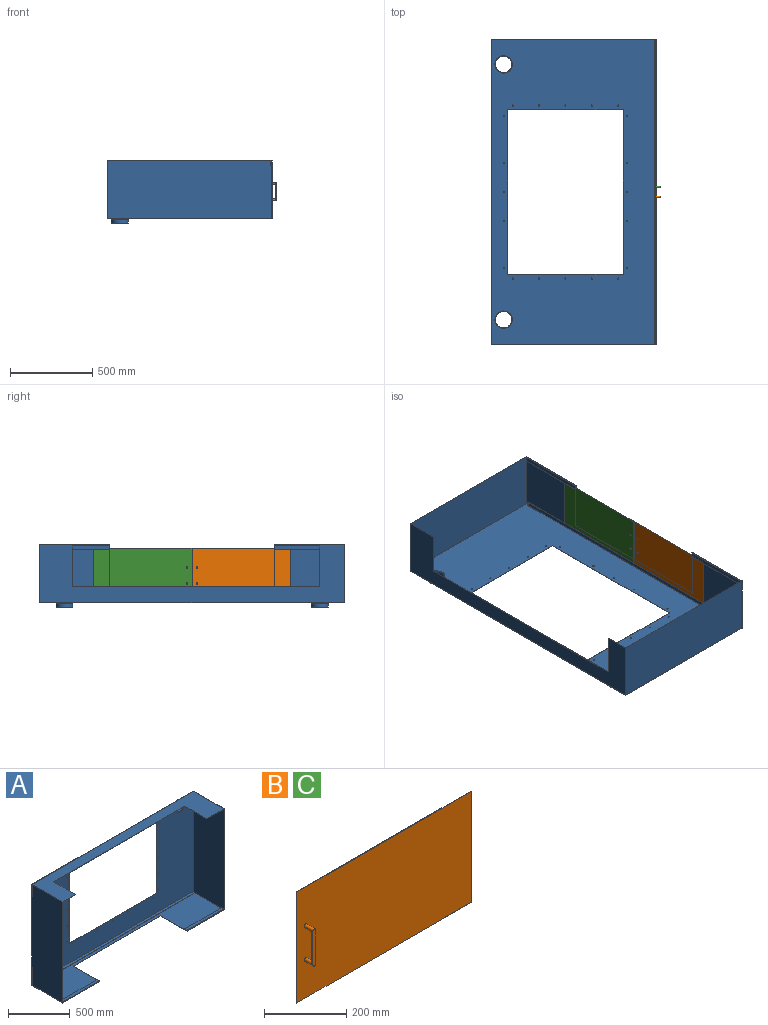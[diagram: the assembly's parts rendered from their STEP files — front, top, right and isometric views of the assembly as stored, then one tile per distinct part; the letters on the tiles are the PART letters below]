
ASSEMBLY  parts=3 mates=2
PART A: 67 faces, bbox 1850x376.5x1000 mm
  f0: plane 1847x350mm, normal (0,0,1), area 343690mm2, adj f2,f3,f34,f36,f37,f41,f42,f43
  f1: plane 1850x351.5mm, normal (0,0,-1), area 348775mm2, adj f2,f4,f5,f33,f37,f41,f42,f43
  f2: plane 1000x425mm, normal (0,-1,0), area 5373mm2, adj f0,f1,f5,f32,f35,f36,f39,f43
  f3: plane 1847x997mm, normal (0,-1,0), area 1117616.6mm2, adj f0,f6,f7,f8,f9,f10,f11,f12
  f4: plane 1000x351.5mm, normal (-1,0,0), area 351500mm2, adj f1,f32,f33,f37
  f5: plane 1000x351.5mm, normal (1,0,0), area 351500mm2, adj f1,f2,f32,f33
  f6: plane 700x1.5mm, normal (1,0,0), area 1050mm2, adj f3,f7,f31,f33
  f7: plane 1000x1.5mm, normal (0,0,-1), area 1500mm2, adj f3,f6,f8,f33
  f8: plane 700x1.5mm, normal (-1,0,0), area 1050mm2, adj f3,f7,f31,f33
  f9: cylinder r=3.5mm len=7mm, axis (0,1,0), area 33mm2, adj f3,f33
  f10: cylinder r=3.5mm len=7mm, axis (0,1,0), area 33mm2, adj f3,f33
  f11: cylinder r=3.5mm len=7mm, axis (0,1,0), area 33mm2, adj f3,f33
  f12: cylinder r=3.5mm len=7mm, axis (0,1,0), area 33mm2, adj f3,f33
  f13: cylinder r=3.5mm len=7mm, axis (0,1,0), area 33mm2, adj f3,f33
  f14: cylinder r=3.5mm len=7mm, axis (0,1,0), area 33mm2, adj f3,f33
  f15: cylinder r=3.5mm len=7mm, axis (0,1,0), area 33mm2, adj f3,f33
  f16: cylinder r=3.5mm len=7mm, axis (0,1,0), area 33mm2, adj f3,f33
  f17: cylinder r=3.5mm len=7mm, axis (0,1,0), area 33mm2, adj f3,f33
  f18: cylinder r=3.5mm len=7mm, axis (0,1,0), area 33mm2, adj f3,f33
  f19: cylinder r=50mm len=100mm, axis (0,1,0), area 7382.7mm2, adj f45,f48
  f20: cylinder r=50mm len=100mm, axis (0,1,0), area 7382.7mm2, adj f47,f49
  f21: cylinder r=3.5mm len=7mm, axis (0,1,0), area 33mm2, adj f3,f33
  f22: cylinder r=3.5mm len=7mm, axis (0,1,0), area 33mm2, adj f3,f33
  f23: cylinder r=3.5mm len=7mm, axis (0,1,0), area 33mm2, adj f3,f33
  f24: cylinder r=3.5mm len=7mm, axis (0,1,0), area 33mm2, adj f3,f33
  f25: cylinder r=3.5mm len=7mm, axis (0,1,0), area 33mm2, adj f3,f33
  f26: cylinder r=3.5mm len=7mm, axis (0,1,0), area 33mm2, adj f3,f33
  f27: cylinder r=3.5mm len=7mm, axis (0,1,0), area 33mm2, adj f3,f33
  f28: cylinder r=3.5mm len=7mm, axis (0,1,0), area 33mm2, adj f3,f33
  f29: cylinder r=3.5mm len=7mm, axis (0,1,0), area 33mm2, adj f3,f33
  f30: cylinder r=3.5mm len=7mm, axis (0,1,0), area 33mm2, adj f3,f33
  f31: plane 1000x1.5mm, normal (0,0,1), area 1500mm2, adj f3,f6,f8,f33
  f32: plane 1850x351.5mm, normal (0,0,1), area 273025mm2, adj f2,f4,f5,f33,f37,f38,f39,f40
  f33: plane 1850x1000mm, normal (0,1,0), area 1131910.7mm2, adj f1,f4,f5,f6,f7,f8,f9,f10
  f34: plane 997x350mm, normal (1,0,0), area 348950mm2, adj f0,f3,f35,f37
  f35: plane 1847x350mm, normal (0,0,-1), area 269200mm2, adj f2,f3,f34,f36,f37,f38,f39,f40
  f36: plane 997x350mm, normal (-1,0,0), area 348950mm2, adj f0,f2,f3,f35
  f37: plane 1000x425mm, normal (0,-1,0), area 5298mm2, adj f0,f1,f4,f32,f34,f35,f40,f41
  f38: plane 1500x1.5mm, normal (0,-1,0), area 2250mm2, adj f32,f35,f39,f40
  f39: plane 251.5x1.5mm, normal (-1,0,0), area 377.3mm2, adj f2,f32,f35,f38
  f40: plane 251.5x1.5mm, normal (1,0,0), area 377.3mm2, adj f32,f35,f37,f38
  f41: plane 301.5x8.5mm, normal (1,0,0), area 537.8mm2, adj f0,f1,f37,f42,f58,f62,f63,f64
  f42: plane 1000x1.5mm, normal (0,-1,0), area 1500mm2, adj f0,f1,f41,f43
  f43: plane 301.5x8.5mm, normal (-1,0,0), area 537.8mm2, adj f0,f1,f2,f42,f55,f59,f60,f61
  f44: cylinder r=51.5mm len=103mm, axis (0,-1,0), area 7604.2mm2, adj f45,f66
  f45: plane 103x103mm, normal (0,1,0), area 478.3mm2, adj f19,f44
  f46: cylinder r=50.5mm len=101mm, axis (0,-1,0), area 7456.6mm2, adj f47,f65
  f47: plane 101x101mm, normal (0,1,0), area 157.9mm2, adj f20,f46
  f48: torus R=53mm, axis (0,-1,0), area 1512.7mm2, adj f3,f19
  f49: torus R=53mm, axis (0,-1,0), area 1512.7mm2, adj f3,f20
  f50: plane 1807.76x25mm, normal (0,0,1), area 45193.9mm2, adj f3,f51,f53,f54
  f51: plane 25x3mm, normal (-1,0,0), area 75mm2, adj f3,f50,f52,f54
  f52: plane 1807.76x25mm, normal (0,0,-1), area 45193.9mm2, adj f3,f51,f53,f54
  f53: plane 25x3mm, normal (1,0,0), area 75mm2, adj f3,f50,f52,f54
  f54: plane 1807.76x3mm, normal (0,-1,0), area 5423.3mm2, adj f50,f51,f52,f53
  f55: plane 420x4mm, normal (0,1,0), area 1680mm2, adj f0,f43,f56,f59
  f56: plane 26.5x7mm, normal (1,0,0), area 85.5mm2, adj f0,f2,f55,f59,f60,f61
  f57: plane 26.5x7mm, normal (-1,0,0), area 85.5mm2, adj f0,f37,f58,f62,f63,f64
  f58: plane 420x4mm, normal (0,1,0), area 1680mm2, adj f0,f41,f57,f62
  f59: plane 420x25mm, normal (0,0,-1), area 10500mm2, adj f43,f55,f56,f61
  f60: plane 420x26.5mm, normal (0,0,1), area 11130mm2, adj f2,f43,f56,f61
  f61: plane 420x3mm, normal (0,1,0), area 1260mm2, adj f43,f56,f59,f60
  f62: plane 420x25mm, normal (0,0,-1), area 10500mm2, adj f41,f57,f58,f64
  f63: plane 420x26.5mm, normal (0,0,1), area 11130mm2, adj f37,f41,f57,f64
  f64: plane 420x3mm, normal (0,1,0), area 1260mm2, adj f41,f57,f62,f63
  f65: torus R=52mm, axis (0,-1,0), area 755.7mm2, adj f33,f46
  f66: torus R=53mm, axis (0,-1,0), area 770.5mm2, adj f33,f44
PART B: 12 faces, bbox 600x31.5x330 mm
  f0: plane 600x1.5mm, normal (0,0,1), area 900mm2, adj f1,f3,f4,f5
  f1: plane 330x1.5mm, normal (-1,0,0), area 495mm2, adj f0,f2,f4,f5
  f2: plane 600x1.5mm, normal (0,0,-1), area 900mm2, adj f1,f3,f4,f5
  f3: plane 330x1.5mm, normal (1,0,0), area 495mm2, adj f0,f2,f4,f5
  f4: plane 600x330mm, normal (0,-1,0), area 197842.9mm2, adj f0,f1,f2,f3,f6,f7
  f5: plane 600x330mm, normal (0,1,0), area 198000mm2, adj f0,f1,f2,f3
  f6: cylinder r=5mm len=30mm, axis (0,1,0), area 863.9mm2, adj f4,f8,f9,f10,f11
  f7: cylinder r=5mm len=30mm, axis (0,1,0), area 863.9mm2, adj f4,f8,f9,f10,f11
  f8: plane 100x10mm, normal (0,1,0), area 921.5mm2, adj f6,f7,f9,f10
  f9: plane 100x5mm, normal (-1,0,0), area 500mm2, adj f6,f7,f8,f11
  f10: plane 100x5mm, normal (1,0,0), area 500mm2, adj f6,f7,f8,f11
  f11: plane 110x10mm, normal (0,-1,0), area 1078.5mm2, adj f6,f7,f9,f10
PART C: same geometry as B
PLACE A rot(axis=(-0.58,-0.58,0.58),120deg) t=(0,0,-27)mm
PLACE B rot(axis=(-0.71,0.71,0),180deg) t=(547,-300,139.5)mm
PLACE C rot(axis=(0,0,1),90deg) t=(547,300,139.5)mm
MATE fastened C.f4 <-> A.f0  axis (1,0,0) through (548.5,600,-25.5)mm
MATE fastened B.f4 <-> A.f0  axis (1,0,0) through (548.5,-600,-25.5)mm
